# Revit family: НЕВАТОМ_Заслонка Э-D-ОЦ-Р.Р., Версия 2
name_source: partatom
category: Арматура воздуховодов
revit_build: Autodesk Revit 2017 (Build: 20170118_1100(x64)
units: mm (PartAtom-declared; Revit-internal decimal feet)

## family parameters
Всегда вертикально = Нет
На основе рабочей плоскости = Нет
Общий = Нет
При загрузке вырезать с полостями = Нет
Размер круглого соединителя = Использовать диаметр
Тип детали = Вставляется

## types (1)
- Заслонка-Э-D-p.p.
    ADSK_Единица измерения = шт.
    ADSK_Завод-изготовитель = НЕВАТОМ
    ADSK_Количество = 1
    ADSK_Количество фаз = 1
    ADSK_Материал наименование = Оцинкованная сталь
    ADSK_Наименование = Заслонка круглого сечения
    ADSK_Напряжение = 220 В
    ADSK_Полная мощность = 0 В·А
    ADSK_Потеря давления воздуха = 0.0 Па
    ADSK_Расход воздуха = 0.0 м³/ч
    ADSK_Ток = 0 А
    Nevatom_URL = https://t.me
    t = 1 мм
    ДЛ.КРЕПЛ = 50 мм
    Закрыто = Нет
    Материал корпуса = Материал корпуса
    Материал уплотнителя = Материал уплотнителя
    Открыто = Да
    дл.площадки = 100 мм
    шп = 60 мм
